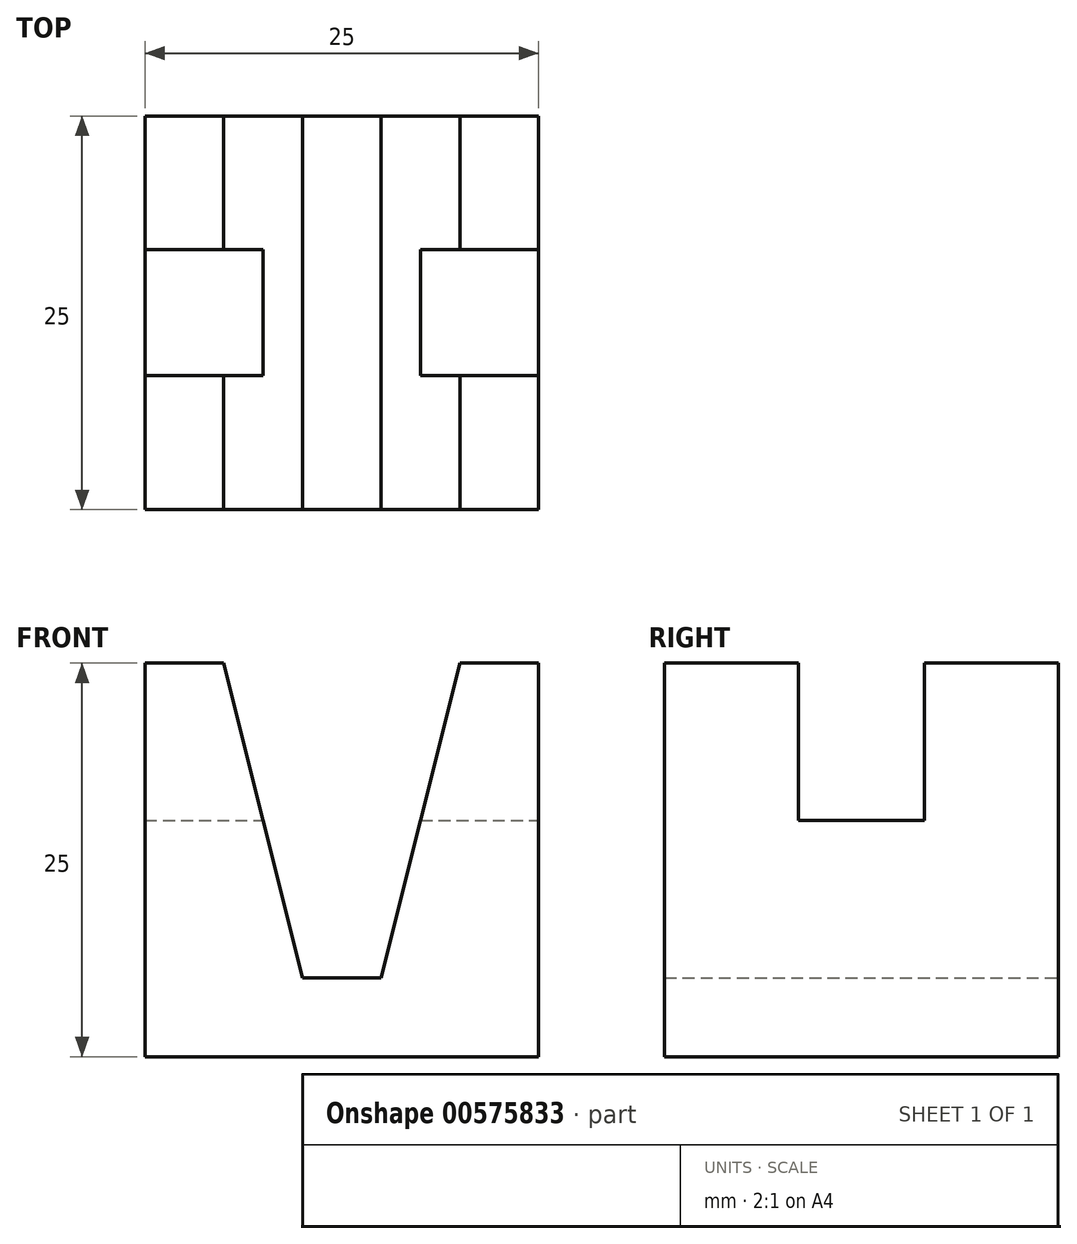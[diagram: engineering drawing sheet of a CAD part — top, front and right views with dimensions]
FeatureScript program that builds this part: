
annotation { "Feature Type Name" : "Feature", "Feature Type Description" : "" }
export const myFeature = defineFeature(function(context is Context, id is Id, definition is map)
    precondition{}
    {
        {
            var Q0;
            Q0=qCreatedBy(makeId("Front.planeOp"),FACE);
            var sketch = newSketch(context, id + "F0", { "sketchPlane" : qUnion([Q0])});
            skLineSegment(sketch, "E0", {"start": v(-12.5, 0) * mm, "end": v(12.5, 0) * mm});
            skLineSegment(sketch, "E1", {"start": v(12.5, 0) * mm, "end": v(12.5, 25) * mm});
            skLineSegment(sketch, "E2", {"start": v(12.5, 25) * mm, "end": v(7.5, 25) * mm});
            skLineSegment(sketch, "E3", {"start": v(-12.5, 25) * mm, "end": v(-12.5, 0) * mm});
            skLineSegment(sketch, "E4", {"start": v(-7.5, 25) * mm, "end": v(-2.5, 5) * mm});
            skLineSegment(sketch, "E5", {"start": v(-2.5, 5) * mm, "end": v(2.5, 5) * mm});
            skLineSegment(sketch, "E6", {"start": v(2.5, 5) * mm, "end": v(7.5, 25) * mm});
            skLineSegment(sketch, "E7.trimOffspring", {"start": v(-7.5, 25) * mm, "end": v(-12.5, 25) * mm});
            skSolve(sketch);
        }
        {
            var Q0;
            Q0=makeQuery(id+"F0.imprint","IMPRINT",FACE,{"disambiguationData":[TD([[makeQuery(id+"F0.imprint","IMPRINT",EDGE,{"derivedFrom":sQuery(id+"F0.wireOp",EDGE,"E0")}),1.0]])]});
            extrude(context, id + "F1", {"entities" : qUnion([Q0]), "depth" : 25 * mm, "offsetDistance" : 25 * mm, "symmetric" : true});
        }
        {
            var Q0;
            Q0=makeQuery(id+"F1.opExtrude","SWEPT_FACE",FACE,{"disambiguationData":[OSD([sQuery(id+"F0.wireOp",EDGE,"E1")])]});
            var sketch = newSketch(context, id + "F2", { "sketchPlane" : qUnion([Q0])});
            skLineSegment(sketch, "E8", {"start": v(-4, 25) * mm, "end": v(-4, 15) * mm});
            skLineSegment(sketch, "E9", {"start": v(-4, 15) * mm, "end": v(4, 15) * mm});
            skLineSegment(sketch, "E10", {"start": v(4, 15) * mm, "end": v(4, 25) * mm});
            skLineSegment(sketch, "E11", {"start": v(4, 25) * mm, "end": v(-4, 25) * mm});
            skSolve(sketch);
        }
        {
            var Q0;
            Q0=makeQuery(id+"F2.imprint","IMPRINT",FACE,{"disambiguationData":[TD([[makeQuery(id+"F2.imprint","IMPRINT",EDGE,{"derivedFrom":sQuery(id+"F2.wireOp",EDGE,"E8")}),1.0]])]});
            extrude(context, id + "F3", {"entities" : qUnion([Q0]), "operationType" : NewBodyOperationType.REMOVE, "endBound" : BoundingType.THROUGH_ALL, "oppositeDirection" : true, "depth" : 25 * mm, "offsetDistance" : 25 * mm});
        }
    });
